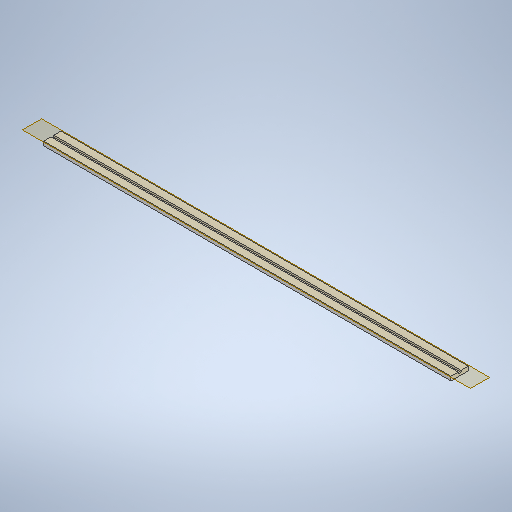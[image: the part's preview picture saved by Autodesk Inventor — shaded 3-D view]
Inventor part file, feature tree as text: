
AUTODESK INVENTOR PART (.ipt)
format: ipt  version: 2025.1 (Build 291241000, 241)  size: 261,632 bytes
history: native  units: mm
features: other x2, extrude x2, sketch x2
ambient origin geometry x8: Origin, YZ Plane, XZ Plane, XY Plane, X Axis, Y Axis, Z Axis, Center Point
bodies: Body1 (feature_tree)
feature tree (6):
  other  "ソリッド1"
  extrude  "押し出し1"  Depth=700.0mm
  other  "作業平面1"
  extrude  "押し出し2"  Depth=30.0mm
  sketch  "スケッチ1"
  sketch  "スケッチ2"
